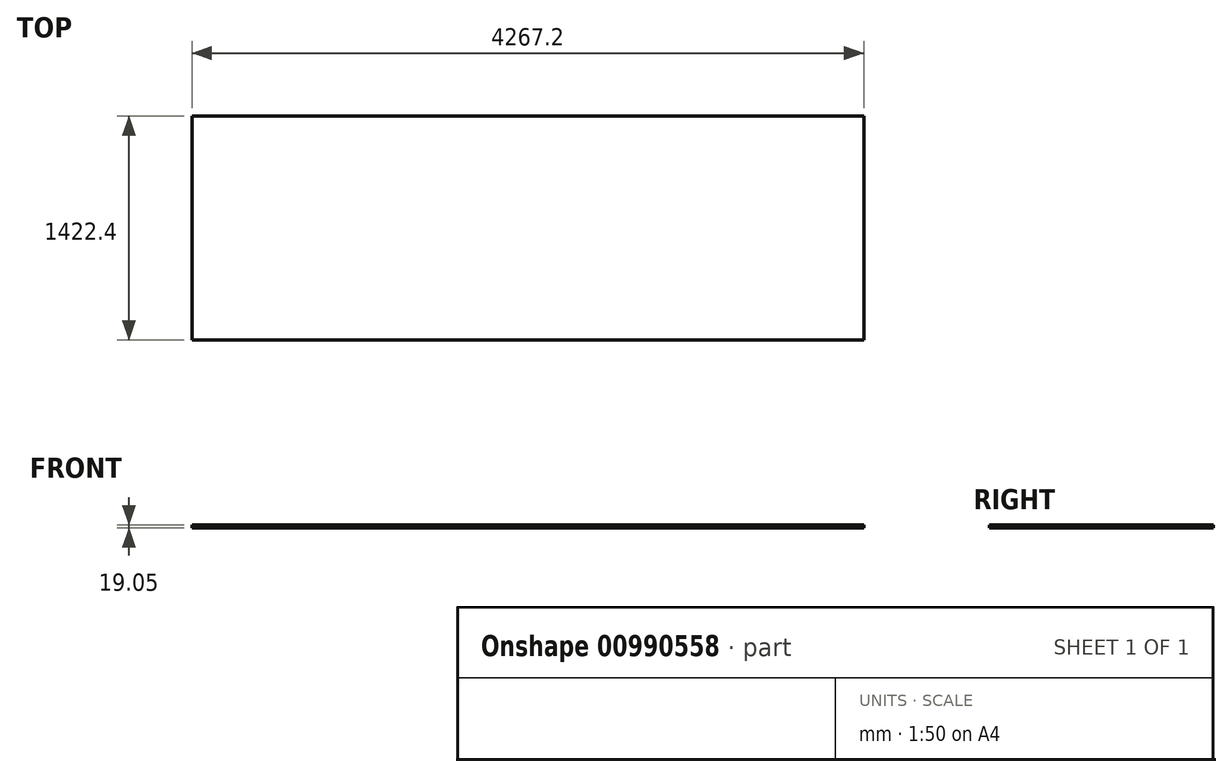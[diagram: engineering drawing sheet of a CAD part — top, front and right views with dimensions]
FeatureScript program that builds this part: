
annotation { "Feature Type Name" : "Feature", "Feature Type Description" : "" }
export const myFeature = defineFeature(function(context is Context, id is Id, definition is map)
    precondition{}
    {
        {
            var Q0;
            Q0=qCreatedBy(makeId("Top.planeOp"),FACE);
            var sketch = newSketch(context, id + "F0", { "sketchPlane" : qUnion([Q0])});
            skLineSegment(sketch, "E0.bottom", {"start": v(-880.03, 274.2) * mm, "end": v(3387.17, 274.2) * mm});
            skLineSegment(sketch, "E0.top", {"start": v(-880.03, -1148.2) * mm, "end": v(3387.17, -1148.2) * mm});
            skLineSegment(sketch, "E0.left", {"start": v(-880.03, 274.2) * mm, "end": v(-880.03, -1148.2) * mm});
            skLineSegment(sketch, "E0.right", {"start": v(3387.17, 274.2) * mm, "end": v(3387.17, -1148.2) * mm});
            skSolve(sketch);
        }
        {
            var Q0;
            Q0=makeQuery(id+"F0.imprint","IMPRINT",FACE,{"disambiguationData":[TD([[makeQuery(id+"F0.imprint","IMPRINT",EDGE,{"derivedFrom":sQuery(id+"F0.wireOp",EDGE,"E0.bottom")}),-1.0]])]});
            extrude(context, id + "F1", {"entities" : qUnion([Q0]), "depth" : 19.05 * mm, "offsetDistance" : 25.4 * mm});
        }
    });
